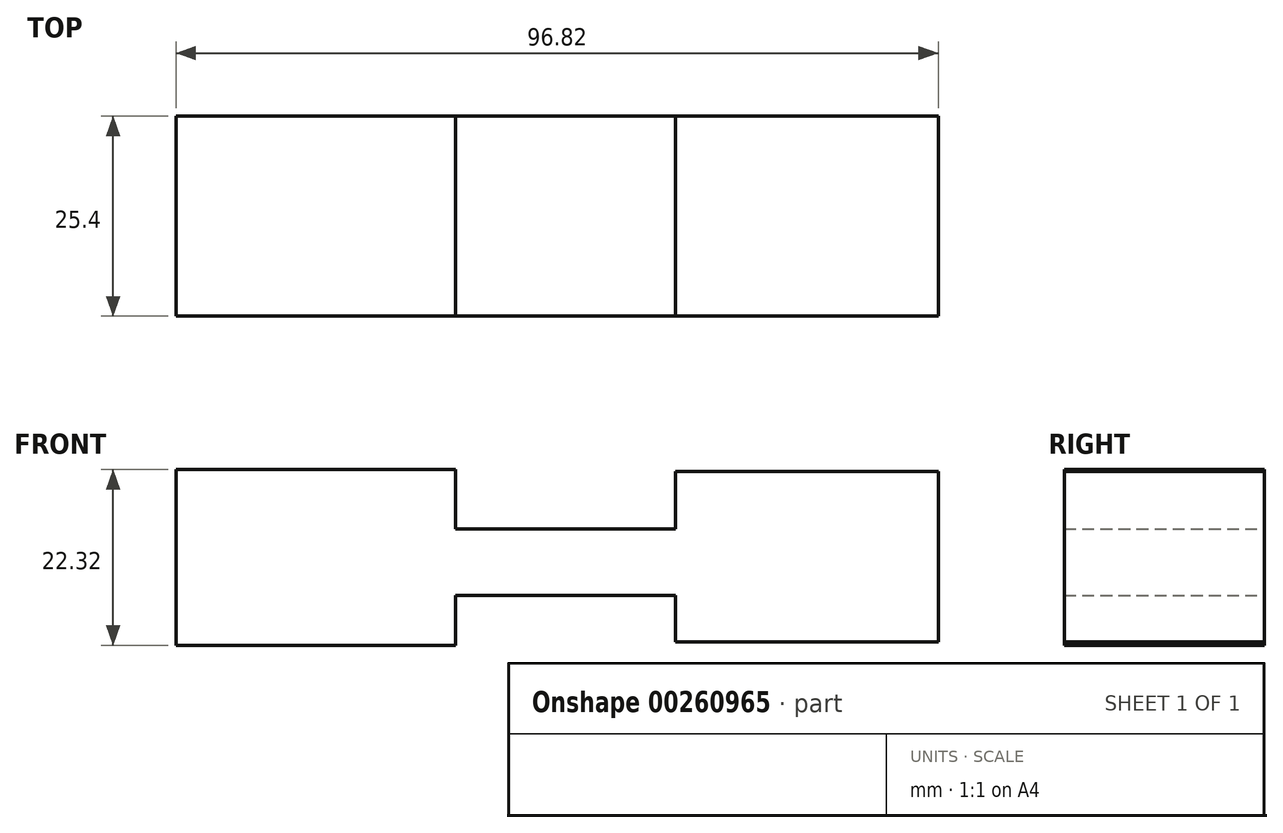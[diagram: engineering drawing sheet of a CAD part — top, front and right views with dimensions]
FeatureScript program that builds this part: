
annotation { "Feature Type Name" : "Feature", "Feature Type Description" : "" }
export const myFeature = defineFeature(function(context is Context, id is Id, definition is map)
    precondition{}
    {
        {
            var Q0;
            Q0=qCreatedBy(makeId("Front.planeOp"),FACE);
            var sketch = newSketch(context, id + "F0", { "sketchPlane" : qUnion([Q0])});
            skLineSegment(sketch, "E0.bottom", {"start": v(-50.76, 46.88) * mm, "end": v(-15.27, 46.88) * mm});
            skLineSegment(sketch, "E0.top", {"start": v(-50.76, 24.56) * mm, "end": v(-15.27, 24.56) * mm});
            skLineSegment(sketch, "E0.left", {"start": v(-50.76, 46.88) * mm, "end": v(-50.76, 24.56) * mm});
            skLineSegment(sketch, "E0.right", {"start": v(-15.27, 46.88) * mm, "end": v(-15.27, 24.56) * mm});
            skLineSegment(sketch, "E1.bottom", {"start": v(12.69, 46.64) * mm, "end": v(46.06, 46.64) * mm});
            skLineSegment(sketch, "E1.top", {"start": v(12.69, 25.03) * mm, "end": v(46.06, 25.03) * mm});
            skLineSegment(sketch, "E1.left", {"start": v(12.69, 46.64) * mm, "end": v(12.69, 25.03) * mm});
            skLineSegment(sketch, "E1.right", {"start": v(46.06, 46.64) * mm, "end": v(46.06, 25.03) * mm});
            skLineSegment(sketch, "E2.bottom", {"start": v(-15.27, 39.36) * mm, "end": v(12.69, 39.36) * mm});
            skLineSegment(sketch, "E2.top", {"start": v(-15.27, 30.9) * mm, "end": v(12.69, 30.9) * mm});
            skLineSegment(sketch, "E2.left", {"start": v(-15.27, 39.36) * mm, "end": v(-15.27, 30.9) * mm});
            skLineSegment(sketch, "E2.right", {"start": v(12.69, 39.36) * mm, "end": v(12.69, 30.9) * mm});
            skSolve(sketch);
        }
        {
            var Q0;
            Q0 = qSketchRegion(id + "F0", true);
            extrude(context, id + "F1", {"entities" : qUnion([Q0]), "depth" : 25.4 * mm});
        }
    });
